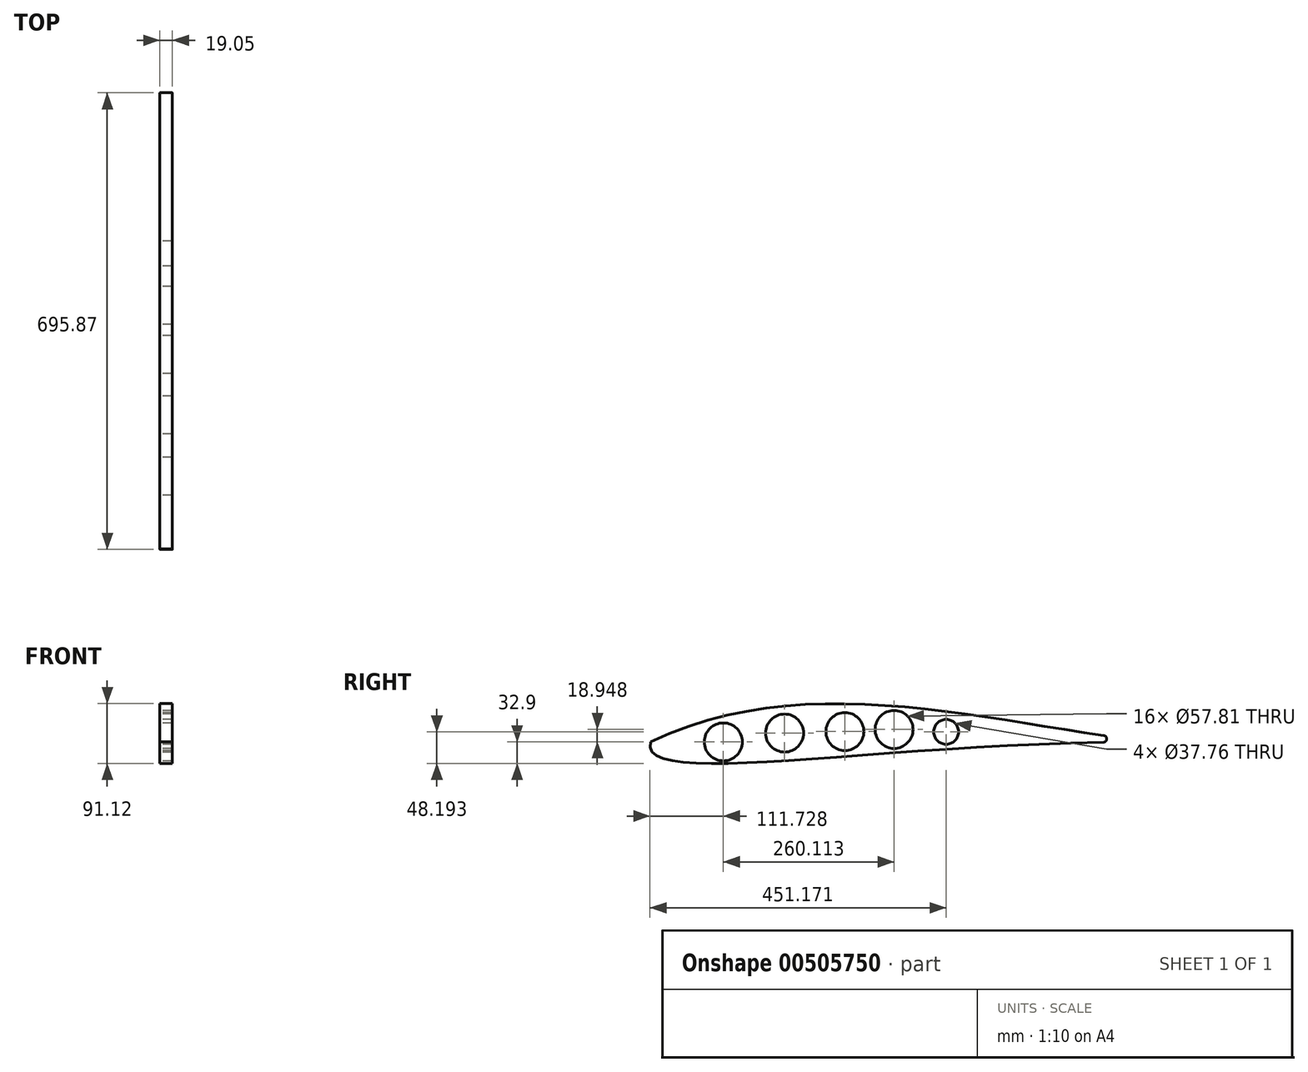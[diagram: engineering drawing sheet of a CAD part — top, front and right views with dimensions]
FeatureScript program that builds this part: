
annotation { "Feature Type Name" : "Feature", "Feature Type Description" : "" }
export const myFeature = defineFeature(function(context is Context, id is Id, definition is map)
    precondition{}
    {
        {
            var Q0;
            Q0=qCreatedBy(makeId("Right.planeOp"),FACE);
            var sketch = newSketch(context, id + "F0", { "sketchPlane" : qUnion([Q0])});
            skLineSegment(sketch, "E0", {"start": v(-242.7, 0) * mm, "end": v(519.3, 0) * mm});
            skFitSpline(sketch, "E1", {"points": [v(519.3, 0) * mm, v(-242.7, 0) * mm], "startDerivative": vector(-750.02, 84.91) * mm, "endDerivative": vector(-728.12, -344.8) * mm});
            skFitSpline(sketch, "E2", {"points": [v(-242.7, 0) * mm, v(519.3, 0) * mm], "startDerivative": vector(-67.51, -223.8) * mm, "endDerivative": vector(1236.84, 0) * mm});
            skCircle(sketch, "E3", {"center": v(-131.95, -0.25) * mm, "radius": 28.9 * mm});
            skPoint(sketch, "E3.first.point", {"position": v(-160.32, -5.8) * mm});
            skPoint(sketch, "E3.second.point", {"position": v(-105.28, 10.88) * mm});
            skPoint(sketch, "E3.third.point", {"position": v(-156.26, 15.4) * mm});
            skCircle(sketch, "E4", {"center": v(-38.64, 13.15) * mm, "radius": 28.9 * mm});
            skCircle(sketch, "E5", {"center": v(53.21, 15.4) * mm, "radius": 28.9 * mm});
            skCircle(sketch, "E6", {"center": v(128.16, 18.7) * mm, "radius": 28.9 * mm});
            skCircle(sketch, "E7", {"center": v(207.5, 15.04) * mm, "radius": 18.88 * mm});
            skSolve(sketch);
        }
        {
            var Q0;
            Q0=makeQuery(id+"F0.imprint","IMPRINT",FACE,{"disambiguationData":[TD([[makeQuery(id+"F0.imprint","IMPRINT",EDGE,{"derivedFrom":sQuery(id+"F0.wireOp",EDGE,"E0")}),-1.0]])]});
            var Q1;
            Q1=makeQuery(id+"F0.imprint","IMPRINT",FACE,{"disambiguationData":[TD([[makeQuery(id+"F0.imprint","IMPRINT",EDGE,{"derivedFrom":sQuery(id+"F0.wireOp",EDGE,"E0")}),1.0]])]});
            extrude(context, id + "F1", {"entities" : qUnion([Q0, Q1]), "depth" : 19.05 * mm});
        }
        {
            var Q0;
            {var subQ0=sQuery(id+"F0.wireOp",EDGE,"E2");var subQ1=sQuery(id+"F0.wireOp",EDGE,"E1");var subQ2=sQuery(id+"F0.wireOp",EDGE,"E0");Q0=makeQuery(id+"F1.opExtrude","SWEPT_EDGE",EDGE,{"disambiguationData":[OSD([subQ2,subQ1,subQ0]),TDD([makeQuery(id+"F0.imprint","INTERSECT",VERTEX,{"disambiguationData":[OD(0.0)],"derivedFrom":[subQ2,subQ1,subQ0]})])]});}
            fillet(context, id + "F2", {"entities" : qUnion([Q0]), "radius" : 5.08 * mm, "tangentPropagation" : true, "allowEdgeOverflow" : false});
        }
    });
